# Revit family: LAMP_DOMO 220 G2 ASYMMETRIC
name_source: partatom
category: Modelos genéricos
revit_build: Autodesk Revit 2015 (Build: 20140606_1530(x64)
units: mm (PartAtom-declared; Revit-internal decimal feet)

## types (3) — shared parameters
CRI = 80
Diameter = 220 mm  [stored 0.721785 ft]
Elevación por defecto = 1219 mm
Fabricante = LAMP
Finish = Matte white
Gear = Electronic
Height = 150 mm
IEE = A+
Initial color = 3000 K
Installation instructions = http://www.lamp.es
Insulation class = II
Lamp = MID-POWER LED
Last update = 29/06/2020
Luminaire type = Indoor - Recessed Downlight
MacAdam = 3
Manufacturer URL = http://www.lamp.es
Manufacturer country = Spain
Manufacturer name = LAMP
Power Supply = 120-240V 50-60Hz
Product URL = http://www.lamp.es
Product datasheet = http://www.lamp.es
Protection rating = IP54
Recessed diameter = 211 mm  [stored 0.692257 ft]
Type = MID POWER NICHIA

## per-type parameters (varying)
| type | Descripción | Efficacy | Initial intensity | LED Lifetime | Modelo | Photometric web file | Plum | Power | Product code | Weight |
| 1534LM 3000 | DOMO 220 G2 ASYM 2000 WW | 67 lm/W | 1534 lm | 50.000 L90 B10 | DO2RD20AS830NW | Cuerpo Domo220 asymmetric : 1534LM 3000 | 23 W | 21 W | DO2RD20AS830NW | 1.54 kg |
| 2110LM 3000 | DOMO 220 G2 ASYM 3000 WW | 66 lm/W | 2110 lm | 50.000 L90 B10 | DO2RD30AS830NW | Cuerpo Domo220 asymmetric : 2110LM 3000 | 32 W | 29 W | DO2RD30AS830NW | 1.54 kg |
| 2737LM 3000 | DOMO 220 G2 ASYM 4000 WW | 68 lm/W | 2737 lm | 50.000 L80 B10 | DO2RD40AS830NW | Cuerpo Domo220 asymmetric : 2737LM 3000 | 41 W | 37 W | DO2RD40AS830NW | 1.62 kg |

note: [stored X ft] marks values corroborated as IEEE doubles in the binary element streams (Revit-internal decimal feet)
